# Revit family: Bedpan_Washer-American_Standard-Straight-6047.861_6047.821
name_source: partatom
category: Plumbing Fixtures
revit_build: Autodesk Revit 2014 (Build: 20130308_1515(x64)
units: mm (PartAtom-declared; Revit-internal decimal feet)

## types (2) — shared parameters
CW Connection = Yes
CWFU = 10
Cold Water Connection Diameter = 1"
Cold Water Connection Height = 24 3/8"
Cold Water Connection Radius = 1/2"
Cold Water Connection Width = 4 1/4"
Default Elevation = 0"
Description = Bedpan Washer Diverted Assembly Kit Offset.
HW Connection = No
Height = 26 3/8"
Installation Type = Surface Mounted
Length = 3"
Manufacturer = American Standard
Material = Metal-American Standard-002-Polished Chrome
Price = Prices may vary. Please consult Manufacturer Representative for most up-to-date price list.
Product Documentation Link = https://www.americanstandard-us.com
Product Page URL = https://www.americanstandard-us.com
Revised Date = 01/18/2017
URL = http://www.americanstandard-us.com
Vent Connection = No
Warranty Information = 1 Year Limited Warranty
Waste Connection = No
Width = 1 1/2"
zero-valued in all types: HWFU, WFU

## per-type parameters (varying)
| type | Flush Rate |
| 6047.821.002 | 1.28 gpf |
| 6047.861.002 | 1.6 gpf |

note: column(s) folded — value = type name in every type: Model

## geometry (parser evidence)
native form markers: Sweep x1
no freeform markers — native parametric forms only
